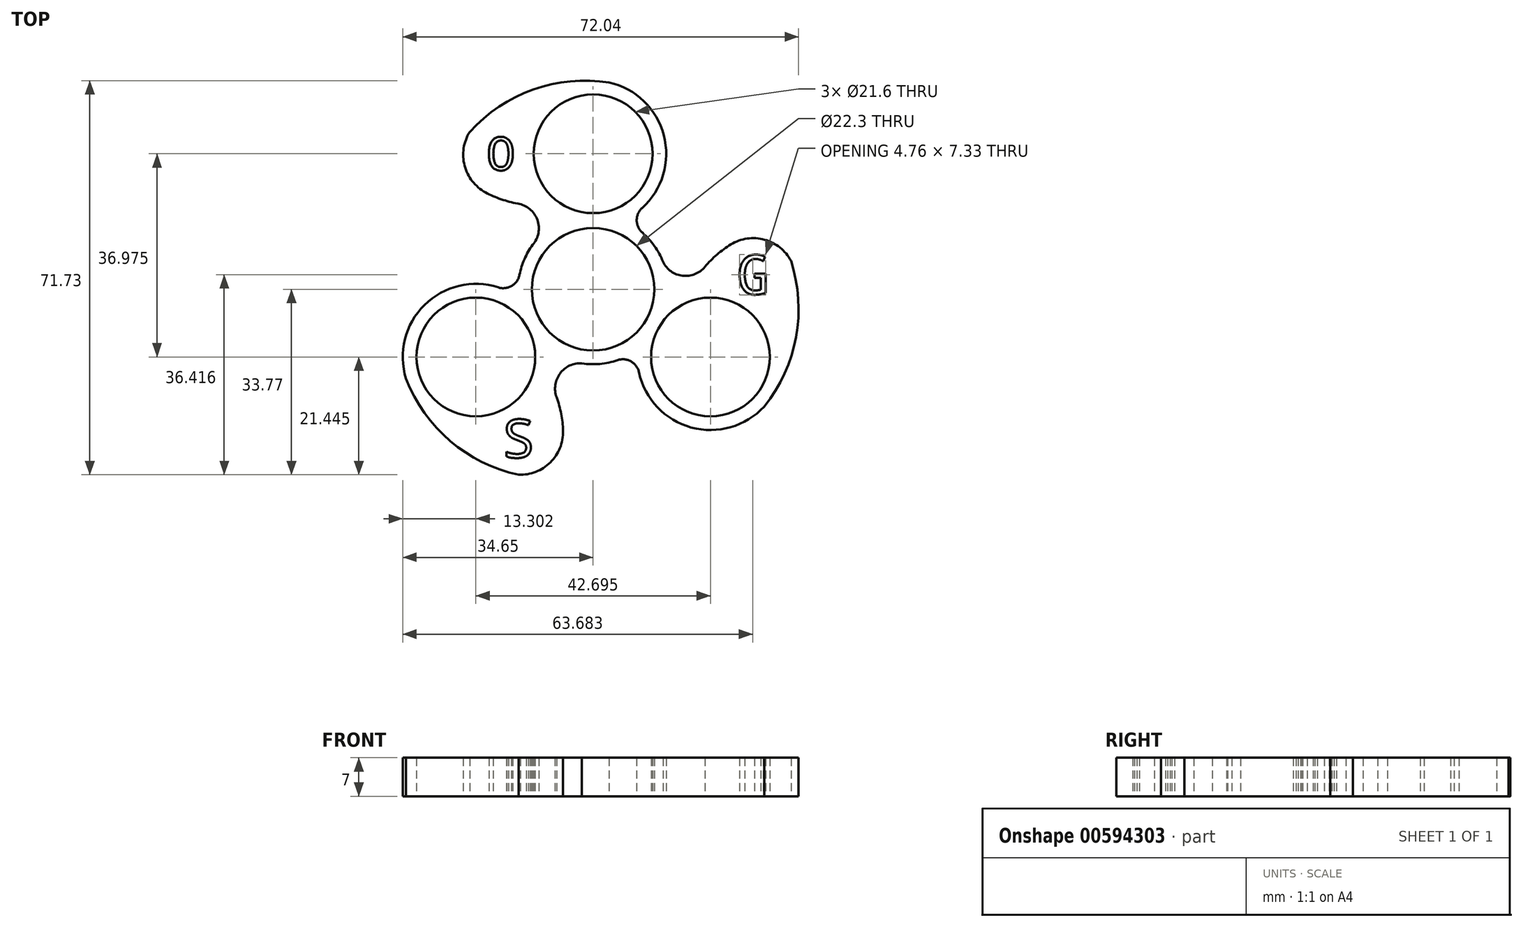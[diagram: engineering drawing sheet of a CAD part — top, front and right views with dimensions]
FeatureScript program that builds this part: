
annotation { "Feature Type Name" : "Feature", "Feature Type Description" : "" }
export const myFeature = defineFeature(function(context is Context, id is Id, definition is map)
    precondition{}
    {
        {
            var Q0;
            Q0=qCreatedBy(makeId("Top.planeOp"),FACE);
            var sketch = newSketch(context, id + "F0", { "sketchPlane" : qUnion([Q0])});
            skCircle(sketch, "E0", {"center": v(0, 0) * mm, "radius": 11.15 * mm});
            skLineSegment(sketch, "E1", {"start": v(0, 0) * mm, "end": v(0, 24.65) * mm});
            skCircle(sketch, "E2", {"center": v(0, 24.65) * mm, "radius": 10.8 * mm});
            skCircle(sketch, "E3.1.0", {"center": v(-21.35, -12.32) * mm, "radius": 10.8 * mm});
            skCircle(sketch, "E3.2.0", {"center": v(21.35, -12.33) * mm, "radius": 10.8 * mm});
            skArc(sketch, "E4.0", {"start": v(8.92, 14.78) * mm, "mid": v(12.86, 28.03) * mm, "end": v(2.92, 37.63) * mm});
            skArc(sketch, "E5.0", {"start": v(-11, 8.07) * mm, "mid": v(-12.5, 5.47) * mm, "end": v(-13.4, 2.61) * mm});
            skArc(sketch, "E6.filletArc", {"start": v(8.92, 14.78) * mm, "mid": v(7.93, 12.53) * mm, "end": v(8.96, 10.3) * mm});
            skArc(sketch, "E7", {"start": v(-11, 8.07) * mm, "mid": v(-10.16, 12.62) * mm, "end": v(-13.71, 15.58) * mm});
            skArc(sketch, "E8", {"start": v(-22.47, 28.6) * mm, "mid": v(-23.4, 22.5) * mm, "end": v(-19.6, 17.63) * mm});
            skArc(sketch, "E9", {"start": v(2.92, 37.63) * mm, "mid": v(-10.92, 36.33) * mm, "end": v(-22.47, 28.6) * mm});
            skArc(sketch, "E10", {"start": v(-19.6, 17.63) * mm, "mid": v(-16.74, 16.37) * mm, "end": v(-13.71, 15.58) * mm});
            skArc(sketch, "E11.1.0", {"start": v(-13.54, -33.77) * mm, "mid": v(-7.79, -31.51) * mm, "end": v(-5.47, -25.79) * mm});
            skArc(sketch, "E11.1.1", {"start": v(-5.47, -25.79) * mm, "mid": v(-5.81, -22.68) * mm, "end": v(-6.64, -19.67) * mm});
            skArc(sketch, "E11.1.2", {"start": v(-1.49, -13.57) * mm, "mid": v(-5.85, -15.1) * mm, "end": v(-6.64, -19.67) * mm});
            skArc(sketch, "E11.1.3", {"start": v(-17.26, 0.33) * mm, "mid": v(-30.7, -2.87) * mm, "end": v(-34.04, -16.29) * mm});
            skArc(sketch, "E11.1.4", {"start": v(-17.26, 0.33) * mm, "mid": v(-14.82, 0.6) * mm, "end": v(-13.4, 2.61) * mm});
            skArc(sketch, "E11.1.5", {"start": v(-34.04, -16.29) * mm, "mid": v(-26, -27.62) * mm, "end": v(-13.54, -33.77) * mm});
            skArc(sketch, "E11.2.0", {"start": v(36.01, 5.16) * mm, "mid": v(31.19, 9.01) * mm, "end": v(25.07, 8.16) * mm});
            skArc(sketch, "E11.2.1", {"start": v(25.07, 8.16) * mm, "mid": v(22.55, 6.3) * mm, "end": v(20.35, 4.08) * mm});
            skArc(sketch, "E11.2.2", {"start": v(12.5, 5.5) * mm, "mid": v(16.01, 2.49) * mm, "end": v(20.35, 4.08) * mm});
            skArc(sketch, "E11.2.3", {"start": v(8.34, -15.12) * mm, "mid": v(17.84, -25.15) * mm, "end": v(31.13, -21.34) * mm});
            skArc(sketch, "E11.2.4", {"start": v(8.34, -15.12) * mm, "mid": v(6.89, -13.13) * mm, "end": v(4.44, -12.9) * mm});
            skArc(sketch, "E11.2.5", {"start": v(31.13, -21.34) * mm, "mid": v(36.92, -8.71) * mm, "end": v(36.01, 5.16) * mm});
            skArc(sketch, "E12.trimOffspring", {"start": v(-2.04, -13.5) * mm, "mid": v(1.23, -13.6) * mm, "end": v(4.44, -12.9) * mm});
            skArc(sketch, "E13.trimOffspring", {"start": v(12.7, 4.98) * mm, "mid": v(11.16, 7.86) * mm, "end": v(8.96, 10.3) * mm});
            skText(sketch, "E14", { "text": "O", "fontName": "DroidSansMono.ttf"});
            skText(sketch, "E15", { "text": "G", "fontName": "DroidSansMono.ttf"});
            skText(sketch, "E16", { "text": "S", "fontName": "DroidSansMono.ttf"});
            const initialGuessF0  = {"E14": [-0.01931, 0.02166, 1, 0, 0.00604], "E15": [0.02608, -0.00092, 1, 0, 0.00719], "E16": [-0.01648, -0.03065, 1, 0, 0.007]};
            skSetInitialGuess(sketch, initialGuessF0);
            skSolve(sketch);
        }
        {
            var Q0;
            Q0 = qSketchRegion(id + "F0", true);
            var Q1;
            Q1=makeQuery(id+"F0.imprint","IMPRINT",FACE,{"disambiguationData":[TD([[makeQuery(id+"F0.imprint","IMPRINT",EDGE,{"derivedFrom":sQuery(id+"F0.wireOp",EDGE,"E0")}),-1.0]])]});
            var Q2;
            Q2=makeQuery(id+"F0.imprint","IMPRINT",FACE,{"disambiguationData":[TD([[makeQuery(id+"F0.imprint","IMPRINT",EDGE,{"derivedFrom":sQuery(id+"F0.wireOp",EDGE,"E14.sketch_text.stroke-6")}),1.0]])]});
            extrude(context, id + "F1", {"entities" : qUnion([Q0, Q1, Q2]), "depth" : 7 * mm, "offsetDistance" : 25 * mm});
        }
    });
